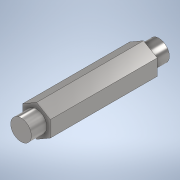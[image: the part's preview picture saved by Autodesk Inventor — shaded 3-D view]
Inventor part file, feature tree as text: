
AUTODESK INVENTOR PART (.ipt)
format: ipt  version: 2020 (Build 240168000, 168)  size: 128,000 bytes
history: native  units: in
note: dims shown in document units (in); Inventor stores cm internally (conversion verified against a paired STEP export)
features: sketch x2, extrude x1, mirror x1, projected_geometry x1
ambient origin geometry x8: Origin, YZ Plane, XZ Plane, XY Plane, X Axis, Y Axis, Z Axis, Center Point
bodies: Solid1 (feature_tree)
feature tree (5):
  extrude  "Extrusion1"  Depth=2.5in TaperAngle=0.0deg
  mirror  "Mirror1"
  sketch  "Sketch1"  dims[d0=0.5in d1=2.5in d2=0.0in]
  sketch  "Sketch4"  dims[d7=0.375in d8=0.281in d9=0.0in]
  projected_geometry  "Projected Loop1"
